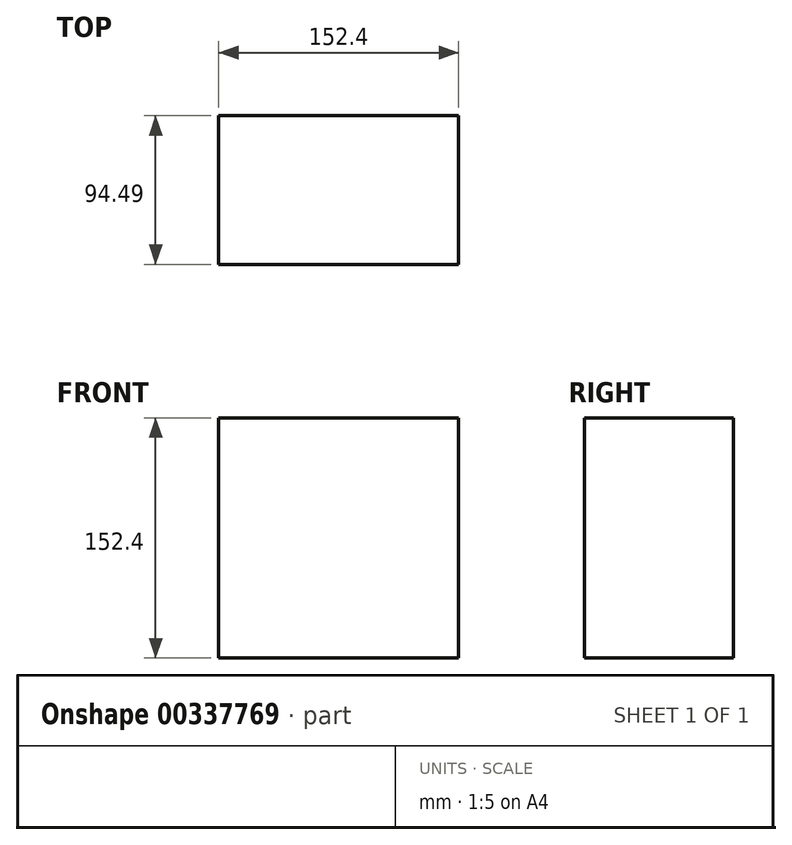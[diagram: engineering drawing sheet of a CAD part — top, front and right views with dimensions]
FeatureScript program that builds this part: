
annotation { "Feature Type Name" : "Feature", "Feature Type Description" : "" }
export const myFeature = defineFeature(function(context is Context, id is Id, definition is map)
    precondition{}
    {
        {
            var Q0;
            Q0=qCreatedBy(makeId("Front.planeOp"),FACE);
            var sketch = newSketch(context, id + "F0", { "sketchPlane" : qUnion([Q0])});
            skLineSegment(sketch, "E0.bottom", {"start": v(-76.2, 76.2) * mm, "end": v(76.2, 76.2) * mm});
            skLineSegment(sketch, "E0.top", {"start": v(-76.2, -76.2) * mm, "end": v(76.2, -76.2) * mm});
            skLineSegment(sketch, "E0.left", {"start": v(-76.2, 76.2) * mm, "end": v(-76.2, -76.2) * mm});
            skLineSegment(sketch, "E0.right", {"start": v(76.2, 76.2) * mm, "end": v(76.2, -76.2) * mm});
            skSolve(sketch);
        }
        {
            var Q0;
            Q0=makeQuery(id+"F0.imprint","IMPRINT",FACE,{"disambiguationData":[TD([[makeQuery(id+"F0.imprint","IMPRINT",EDGE,{"derivedFrom":sQuery(id+"F0.wireOp",EDGE,"E0.bottom")}),-1.0]])]});
            extrude(context, id + "F1", {"entities" : qUnion([Q0]), "depth" : 94.49 * mm});
        }
    });
